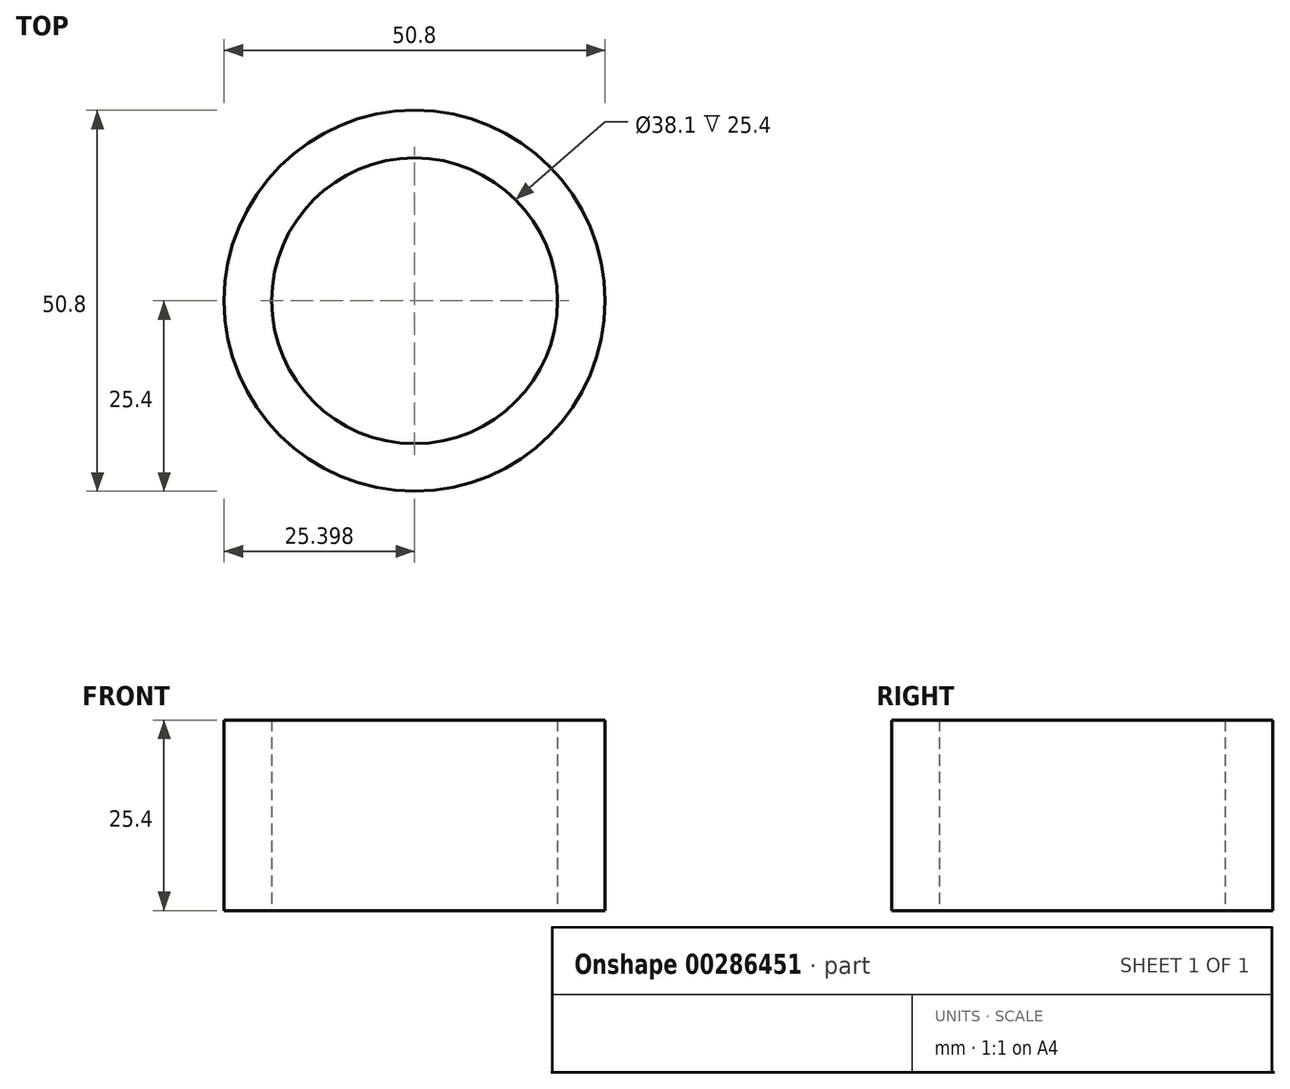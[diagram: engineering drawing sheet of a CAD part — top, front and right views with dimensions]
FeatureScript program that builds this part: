
annotation { "Feature Type Name" : "Feature", "Feature Type Description" : "" }
export const myFeature = defineFeature(function(context is Context, id is Id, definition is map)
    precondition{}
    {
        {
            var Q0;
            Q0=qCreatedBy(makeId("Top.planeOp"),FACE);
            var sketch = newSketch(context, id + "F0", { "sketchPlane" : qUnion([Q0])});
            skCircle(sketch, "E0", {"center": v(-71.51, 0) * mm, "radius": 19.05 * mm});
            skCircle(sketch, "E1", {"center": v(-71.51, 0) * mm, "radius": 25.4 * mm});
            skArc(sketch, "E2", {"start": v(-33.41, 6.35) * mm, "mid": v(-39.76, 0) * mm, "end": v(-33.41, -6.35) * mm});
            skArc(sketch, "E3", {"start": v(17.39, -6.35) * mm, "mid": v(23.74, 0) * mm, "end": v(17.39, 6.35) * mm});
            skCircle(sketch, "E4", {"center": v(55.49, 0) * mm, "radius": 6.35 * mm});
            skCircle(sketch, "E5", {"center": v(55.49, 0) * mm, "radius": 12.7 * mm});
            skLineSegment(sketch, "E6", {"start": v(-33.41, 6.35) * mm, "end": v(17.39, 6.35) * mm});
            skLineSegment(sketch, "E7", {"start": v(-33.41, -6.35) * mm, "end": v(17.39, -6.35) * mm});
            skLineSegment(sketch, "E8", {"start": v(-68.97, 25.27) * mm, "end": v(56.76, 12.64) * mm});
            skLineSegment(sketch, "E9", {"start": v(56.76, -12.64) * mm, "end": v(-68.97, -25.27) * mm});
            skSolve(sketch);
        }
        {
            var Q0;
            Q0=makeQuery(id+"F0.imprint","IMPRINT",FACE,{"disambiguationData":[TD([[makeQuery(id+"F0.imprint","IMPRINT",EDGE,{"derivedFrom":sQuery(id+"F0.wireOp",EDGE,"E0")}),-1.0]])]});
            extrude(context, id + "F1", {"entities" : qUnion([Q0]), "depth" : 25.4 * mm});
        }
    });
